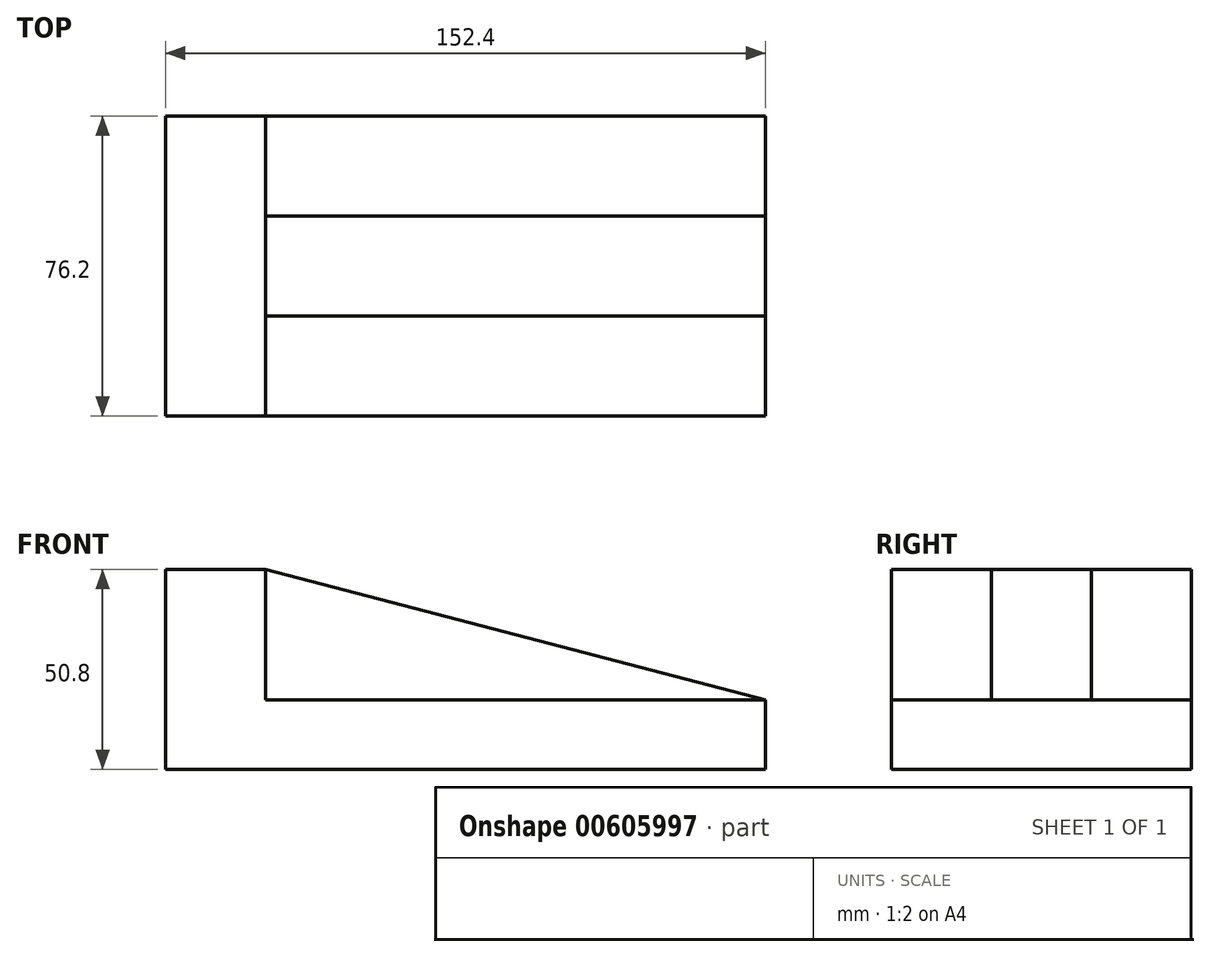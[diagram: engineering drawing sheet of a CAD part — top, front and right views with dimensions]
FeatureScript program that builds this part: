
annotation { "Feature Type Name" : "Feature", "Feature Type Description" : "" }
export const myFeature = defineFeature(function(context is Context, id is Id, definition is map)
    precondition{}
    {
        {
            var Q0;
            Q0=qCreatedBy(makeId("Front.planeOp"),FACE);
            var sketch = newSketch(context, id + "F0", { "sketchPlane" : qUnion([Q0])});
            skLineSegment(sketch, "E0", {"start": v(0, 0) * mm, "end": v(0, 50.8) * mm});
            skLineSegment(sketch, "E1", {"start": v(0, 50.8) * mm, "end": v(25.4, 50.8) * mm});
            skLineSegment(sketch, "E2", {"start": v(25.4, 50.8) * mm, "end": v(152.4, 17.72) * mm});
            skLineSegment(sketch, "E3", {"start": v(152.4, 17.72) * mm, "end": v(152.4, 0) * mm});
            skLineSegment(sketch, "E4", {"start": v(152.4, 0) * mm, "end": v(0, 0) * mm});
            skSolve(sketch);
        }
        {
            var Q0;
            Q0=makeQuery(id+"F0.imprint","IMPRINT",FACE,{"disambiguationData":[TD([[makeQuery(id+"F0.imprint","IMPRINT",EDGE,{"derivedFrom":sQuery(id+"F0.wireOp",EDGE,"E0")}),-1.0]])]});
            extrude(context, id + "F1", {"entities" : qUnion([Q0]), "oppositeDirection" : true, "depth" : 76.2 * mm, "offsetDistance" : 25.4 * mm});
        }
        {
            var Q0;
            Q0=makeQuery(id+"F1.opExtrude","CAP_FACE",FACE,{"disambiguationData":[OSD([sQuery(id+"F0.wireOp",EDGE,"E0"),sQuery(id+"F0.wireOp",EDGE,"E1"),sQuery(id+"F0.wireOp",EDGE,"E2"),sQuery(id+"F0.wireOp",EDGE,"E3"),sQuery(id+"F0.wireOp",EDGE,"E4")])],"isStart":true});
            var sketch = newSketch(context, id + "F2", { "sketchPlane" : qUnion([Q0])});
            skLineSegment(sketch, "E5", {"start": v(152.4, 17.72) * mm, "end": v(25.4, 17.72) * mm});
            skLineSegment(sketch, "E6", {"start": v(25.4, 17.72) * mm, "end": v(25.4, 50.8) * mm});
            skLineSegment(sketch, "E7", {"start": v(25.4, 50.8) * mm, "end": v(152.4, 17.72) * mm});
            skSolve(sketch);
        }
        {
            var Q0;
            Q0=makeQuery(id+"F2.imprint","IMPRINT",FACE,{"disambiguationData":[TD([[makeQuery(id+"F2.imprint","IMPRINT",EDGE,{"derivedFrom":sQuery(id+"F2.wireOp",EDGE,"E5")}),-1.0]])]});
            extrude(context, id + "F3", {"entities" : qUnion([Q0]), "operationType" : NewBodyOperationType.REMOVE, "oppositeDirection" : true, "depth" : 25.4 * mm, "offsetDistance" : 25.4 * mm});
        }
        {
            var Q0;
            Q0=makeQuery(id+"F1.opExtrude","CAP_FACE",FACE,{"disambiguationData":[OSD([sQuery(id+"F0.wireOp",EDGE,"E0"),sQuery(id+"F0.wireOp",EDGE,"E1"),sQuery(id+"F0.wireOp",EDGE,"E2"),sQuery(id+"F0.wireOp",EDGE,"E3"),sQuery(id+"F0.wireOp",EDGE,"E4")])],"isStart":false});
            var sketch = newSketch(context, id + "F4", { "sketchPlane" : qUnion([Q0])});
            skLineSegment(sketch, "E8", {"start": v(-152.4, 17.72) * mm, "end": v(-25.4, 17.72) * mm});
            skLineSegment(sketch, "E9", {"start": v(-25.4, 17.72) * mm, "end": v(-25.4, 50.8) * mm});
            skLineSegment(sketch, "E10", {"start": v(-25.4, 50.8) * mm, "end": v(-152.4, 17.72) * mm});
            skSolve(sketch);
        }
        {
            var Q0;
            Q0=makeQuery(id+"F4.imprint","IMPRINT",FACE,{"disambiguationData":[TD([[makeQuery(id+"F4.imprint","IMPRINT",EDGE,{"derivedFrom":sQuery(id+"F4.wireOp",EDGE,"E8")}),1.0]])]});
            extrude(context, id + "F5", {"entities" : qUnion([Q0]), "operationType" : NewBodyOperationType.REMOVE, "oppositeDirection" : true, "depth" : 25.4 * mm, "offsetDistance" : 25.4 * mm});
        }
    });
